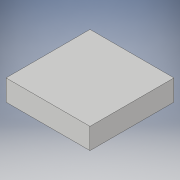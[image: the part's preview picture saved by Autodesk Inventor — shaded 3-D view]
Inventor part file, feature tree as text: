
AUTODESK INVENTOR PART (.ipt)
format: ipt  version: 2019 (Build 230136000, 136)  size: 211,456 bytes
history: native  units: mm
features: extrude x1, sketch x1
ambient origin geometry x8: Origin, YZ Plane, XZ Plane, XY Plane, X Axis, Y Axis, Z Axis, Center Point
bodies: Solid1 (feature_tree)
feature tree (2):
  extrude  "Extrusion1"  Depth=20.0mm
  sketch  "Sketch1"  dims[d0=20.0mm d1=20.0mm d2=5.0mm d3=0.0mm]
